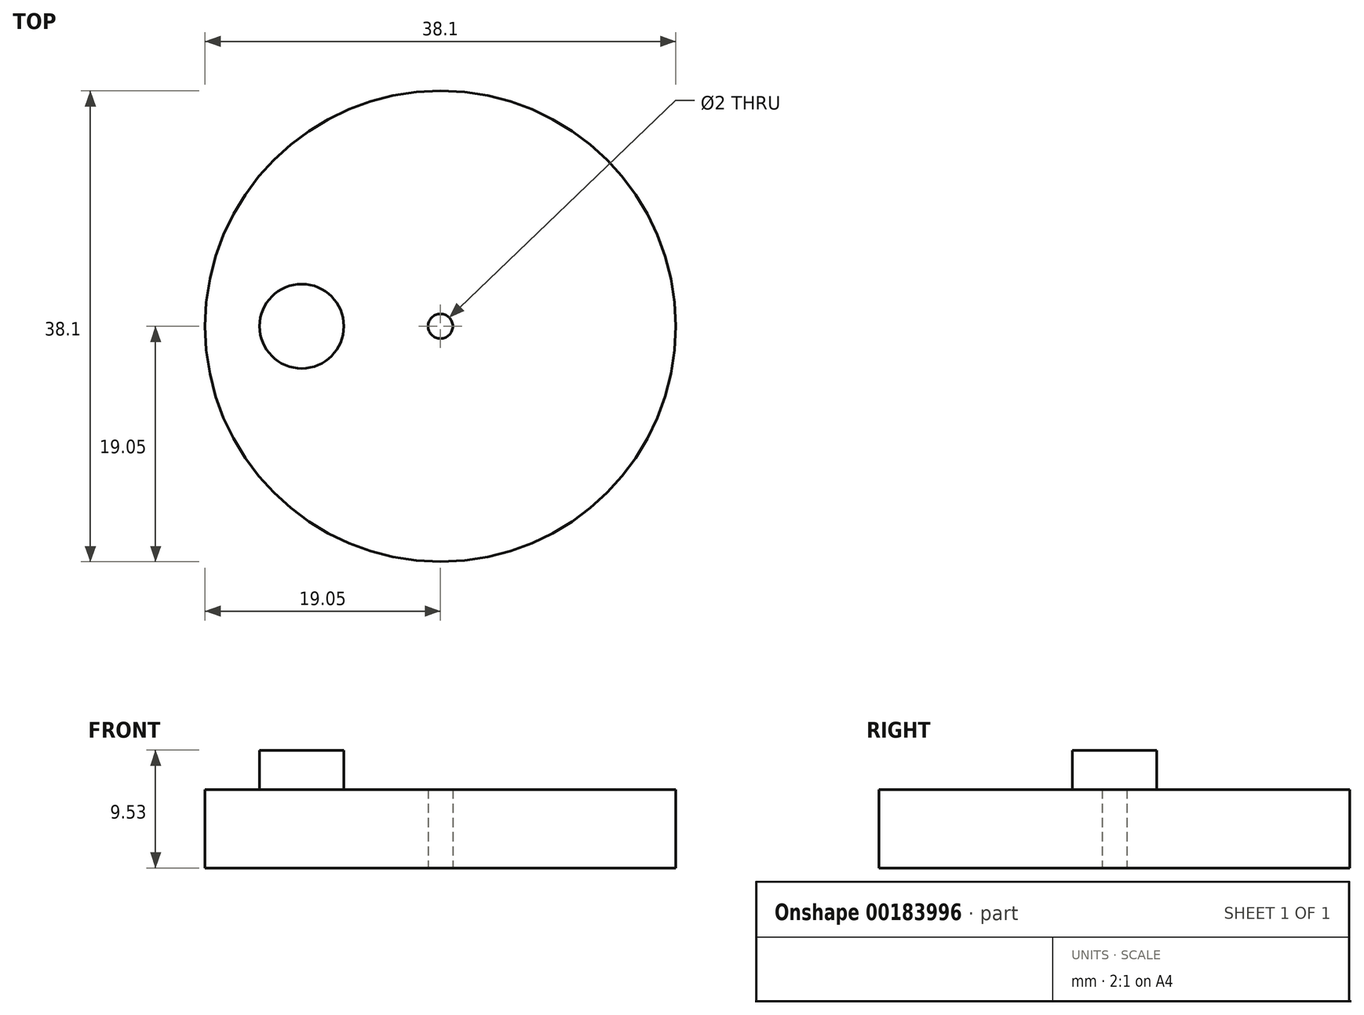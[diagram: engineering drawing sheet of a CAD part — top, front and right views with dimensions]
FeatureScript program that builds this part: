
annotation { "Feature Type Name" : "Feature", "Feature Type Description" : "" }
export const myFeature = defineFeature(function(context is Context, id is Id, definition is map)
    precondition{}
    {
        {
            var Q0;
            Q0=qCreatedBy(makeId("Top.planeOp"),FACE);
            var sketch = newSketch(context, id + "F0", { "sketchPlane" : qUnion([Q0])});
            skCircle(sketch, "E0", {"center": v(0, 0) * mm, "radius": 19.05 * mm});
            skCircle(sketch, "E1", {"center": v(0, 0) * mm, "radius": 1 * mm});
            skSolve(sketch);
        }
        {
            var Q0;
            Q0=makeQuery(id+"F0.imprint","IMPRINT",FACE,{"disambiguationData":[TD([[makeQuery(id+"F0.imprint","IMPRINT",EDGE,{"derivedFrom":sQuery(id+"F0.wireOp",EDGE,"E0")}),1.0]])]});
            extrude(context, id + "F1", {"entities" : qUnion([Q0]), "depth" : 6.35 * mm});
        }
        {
            var Q0;
            Q0=makeQuery(id+"F1.opExtrude","CAP_FACE",FACE,{"disambiguationData":[OSD([sQuery(id+"F0.wireOp",EDGE,"E0"),sQuery(id+"F0.wireOp",EDGE,"E1")])],"isStart":false});
            var sketch = newSketch(context, id + "F2", { "sketchPlane" : qUnion([Q0])});
            skCircle(sketch, "E2", {"center": v(-11.23, 0) * mm, "radius": 3.41 * mm});
            skSolve(sketch);
        }
        {
            var Q0;
            Q0 = qSketchRegion(id + "F2", true);
            extrude(context, id + "F3", {"entities" : qUnion([Q0]), "operationType" : NewBodyOperationType.ADD, "depth" : 3.17 * mm});
        }
    });
